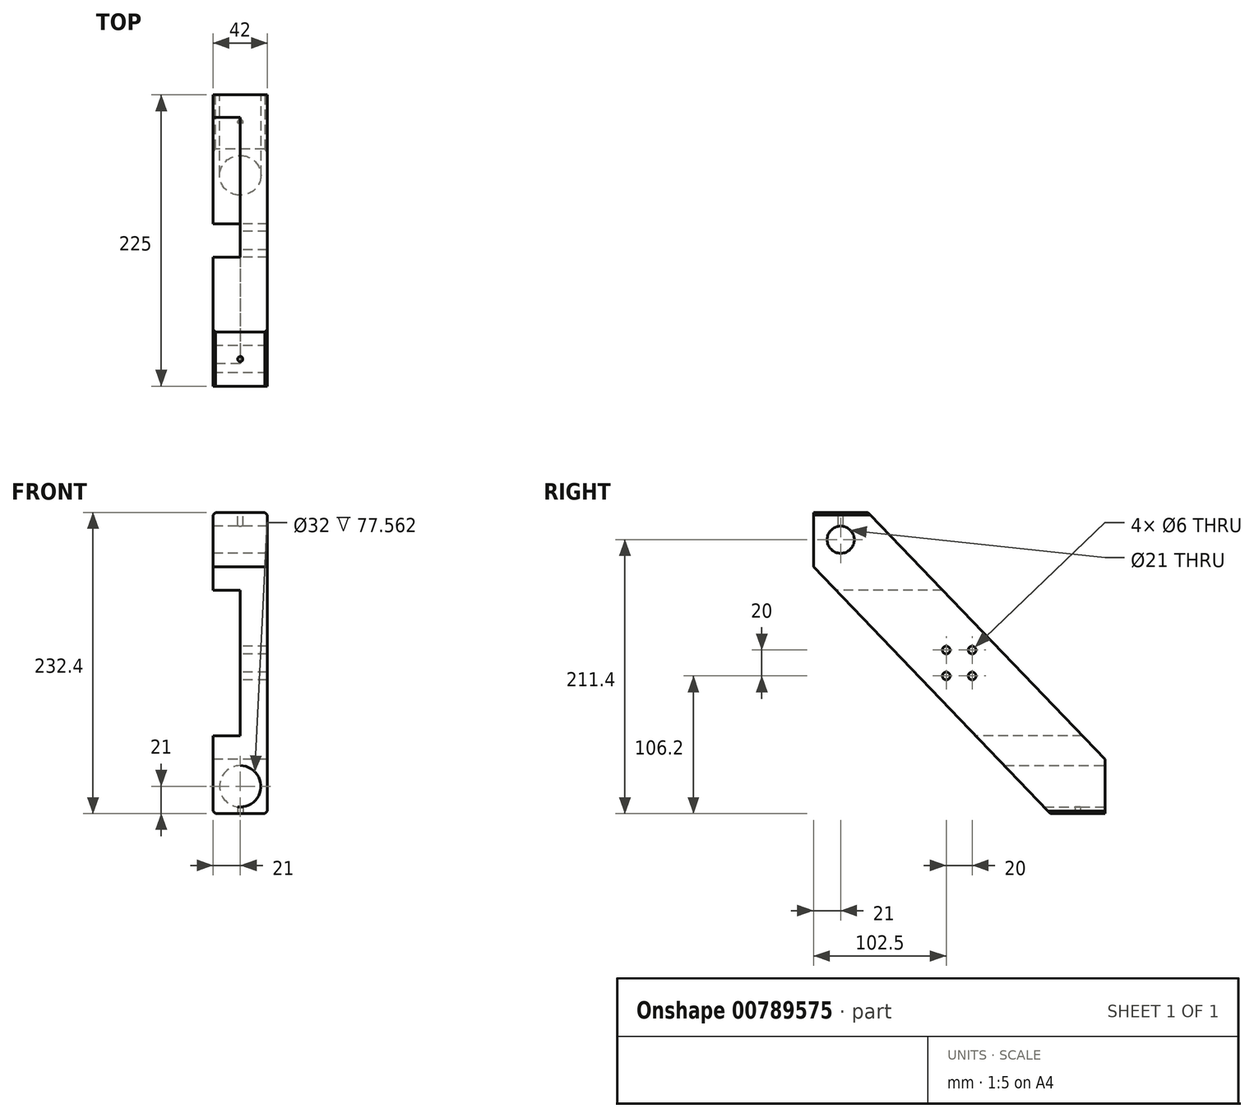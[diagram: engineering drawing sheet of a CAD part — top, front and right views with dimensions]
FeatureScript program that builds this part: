
annotation { "Feature Type Name" : "Feature", "Feature Type Description" : "" }
export const myFeature = defineFeature(function(context is Context, id is Id, definition is map)
    precondition{}
    {
        {
            var Q0;
            Q0=qCreatedBy(makeId("Right.planeOp"),FACE);
            var sketch = newSketch(context, id + "F0", { "sketchPlane" : qUnion([Q0])});
            skLineSegment(sketch, "E0.top", {"start": v(112.5, -116.2) * mm, "end": v(70.5, -116.2) * mm});
            skLineSegment(sketch, "E0.right", {"start": v(-112.5, 116.2) * mm, "end": v(-112.5, 74.2) * mm});
            skCircle(sketch, "E1", {"center": v(-91.5, 95.2) * mm, "radius": 10.5 * mm});
            skPoint(sketch, "E2", {"position": v(0, 0) * mm});
            skPoint(sketch, "E3.trimOffspring.end.orphan", {"position": v(-112.5, 116.2) * mm});
            skPoint(sketch, "E4", {"position": v(70.5, -116.2) * mm});
            skPoint(sketch, "E5", {"position": v(112.5, -74.2) * mm});
            skPoint(sketch, "E6", {"position": v(-112.5, 74.2) * mm});
            skLineSegment(sketch, "E7", {"start": v(70.5, -116.2) * mm, "end": v(-112.5, 74.2) * mm});
            skPoint(sketch, "E8", {"position": v(-70.5, 116.2) * mm});
            skLineSegment(sketch, "E9", {"start": v(112.5, -74.2) * mm, "end": v(-70.5, 116.2) * mm});
            skLineSegment(sketch, "E10.trimOffspring", {"start": v(-70.5, 116.2) * mm, "end": v(-112.5, 116.2) * mm});
            skLineSegment(sketch, "E11.trimOffspring", {"start": v(112.5, -74.2) * mm, "end": v(112.5, -116.2) * mm});
            skPoint(sketch, "E12", {"position": v(10, 10) * mm});
            skPoint(sketch, "E13", {"position": v(10, -10) * mm});
            skPoint(sketch, "E14", {"position": v(-10, -10) * mm});
            skPoint(sketch, "E15", {"position": v(-10, 10) * mm});
            skCircle(sketch, "E16", {"center": v(10, 10) * mm, "radius": 3 * mm});
            skCircle(sketch, "E17", {"center": v(-10, 10) * mm, "radius": 3 * mm});
            skCircle(sketch, "E18", {"center": v(10, -10) * mm, "radius": 3 * mm});
            skCircle(sketch, "E19", {"center": v(-10, -10) * mm, "radius": 3 * mm});
            skSolve(sketch);
        }
        {
            var Q0;
            Q0=makeQuery(id+"F0.imprint","IMPRINT",FACE,{"disambiguationData":[TD([[makeQuery(id+"F0.imprint","IMPRINT",EDGE,{"derivedFrom":sQuery(id+"F0.wireOp",EDGE,"E0.top")}),-1.0]])]});
            extrude(context, id + "F1", {"entities" : qUnion([Q0]), "depth" : 42 * mm, "offsetDistance" : 25 * mm});
        }
        {
            var Q0;
            Q0=makeQuery(id+"F0.imprint","IMPRINT",FACE,{"disambiguationData":[TD([[makeQuery(id+"F0.imprint","IMPRINT",EDGE,{"derivedFrom":sQuery(id+"F0.wireOp",EDGE,"E0.top")}),-1.0]])]});
            var sketch = newSketch(context, id + "F2", { "sketchPlane" : qUnion([Q0])});
            skLineSegment(sketch, "E20", {"start": v(95.2, -56.2) * mm, "end": v(12.83, -56.2) * mm});
            skLineSegment(sketch, "E21", {"start": v(-12.83, 56.2) * mm, "end": v(-95.2, 56.2) * mm});
            skLineSegment(sketch, "E22", {"start": v(12.83, -56.2) * mm, "end": v(-95.2, 56.2) * mm});
            skLineSegment(sketch, "E23", {"start": v(-12.83, 56.2) * mm, "end": v(95.2, -56.2) * mm});
            skSolve(sketch);
        }
        {
            var Q0;
            Q0=makeQuery(id+"F2.imprint","IMPRINT",FACE,{"disambiguationData":[TD([[makeQuery(id+"F2.imprint","IMPRINT",EDGE,{"derivedFrom":sQuery(id+"F2.wireOp",EDGE,"E20")}),-1.0]])]});
            extrude(context, id + "F3", {"entities" : qUnion([Q0]), "operationType" : NewBodyOperationType.REMOVE, "depth" : 21 * mm, "offsetDistance" : 25 * mm});
        }
        {
            var Q0;
            Q0=makeQuery(id+"F1.opExtrude","SWEPT_FACE",FACE,{"disambiguationData":[OSD([sQuery(id+"F0.wireOp",EDGE,"E11.trimOffspring")])]});
            var sketch = newSketch(context, id + "F4", { "sketchPlane" : qUnion([Q0])});
            skPoint(sketch, "E24", {"position": v(-21, -95.2) * mm});
            skPoint(sketch, "E24.positionSnap0", {"position": v(-42, -95.2) * mm});
            skPoint(sketch, "E24.positionSnap1", {"position": v(-21, -116.2) * mm});
            skCircle(sketch, "E25", {"center": v(-21, -95.2) * mm, "radius": 16 * mm});
            skSolve(sketch);
        }
        {
            var Q0;
            Q0=makeQuery(id+"F4.imprint","IMPRINT",FACE,{"disambiguationData":[TD([[makeQuery(id+"F4.imprint","IMPRINT",EDGE,{"derivedFrom":sQuery(id+"F4.wireOp",EDGE,"E25")}),1.0]])]});
            extrude(context, id + "F5", {"entities" : qUnion([Q0]), "operationType" : NewBodyOperationType.REMOVE, "oppositeDirection" : true, "depth" : 85 * mm, "offsetDistance" : 25 * mm});
        }
        {
            var Q0;
            Q0=makeQuery(id+"F3.boolean.opBoolean","COPY",EDGE,{"derivedFrom":makeQuery(id+"F3.opExtrude","CAP_EDGE",EDGE,{"disambiguationData":[OSD([sQuery(id+"F2.wireOp",EDGE,"E23")])],"isStart":false})});
            var Q1;
            Q1=makeQuery(id+"F3.boolean.opBoolean","COPY",EDGE,{"derivedFrom":makeQuery(id+"F3.opExtrude","CAP_EDGE",EDGE,{"disambiguationData":[OSD([sQuery(id+"F2.wireOp",EDGE,"E22")])],"isStart":false})});
            var Q2;
            Q2=makeQuery(id+"F3.boolean.opBoolean","COPY",EDGE,{"derivedFrom":makeQuery(id+"F3.opExtrude","CAP_EDGE",EDGE,{"disambiguationData":[OSD([sQuery(id+"F2.wireOp",EDGE,"E21")])],"isStart":true})});
            var Q3;
            Q3=makeQuery(id+"F1.opExtrude","CAP_EDGE",EDGE,{"disambiguationData":[OSD([sQuery(id+"F0.wireOp",EDGE,"E10.trimOffspring")])],"isStart":true});
            var Q4;
            Q4=makeQuery(id+"F1.opExtrude","CAP_EDGE",EDGE,{"disambiguationData":[OSD([sQuery(id+"F0.wireOp",EDGE,"E0.top")])],"isStart":true});
            var Q5;
            Q5=makeQuery(id+"F3.boolean.opBoolean","COPY",EDGE,{"derivedFrom":makeQuery(id+"F3.opExtrude","CAP_EDGE",EDGE,{"disambiguationData":[OSD([sQuery(id+"F2.wireOp",EDGE,"E20")])],"isStart":true})});
            var Q6;
            Q6=makeQuery(id+"F1.opExtrude","CAP_EDGE",EDGE,{"disambiguationData":[OSD([sQuery(id+"F0.wireOp",EDGE,"E0.top")])],"isStart":false});
            var Q7;
            Q7=makeQuery(id+"F1.opExtrude","CAP_EDGE",EDGE,{"disambiguationData":[OSD([sQuery(id+"F0.wireOp",EDGE,"E10.trimOffspring")])],"isStart":false});
            chamfer(context, id + "F6", {"entities" : qUnion([Q0, Q1, Q2, Q3, Q4, Q5, Q6, Q7]), "width" : 2 * mm, "tangentPropagation" : true});
        }
        {
            var Q0;
            Q0=makeQuery(id+"F1.opExtrude","SWEPT_FACE",FACE,{"disambiguationData":[OSD([sQuery(id+"F0.wireOp",EDGE,"E10.trimOffspring")])]});
            var sketch = newSketch(context, id + "F7", { "sketchPlane" : qUnion([Q0])});
            skPoint(sketch, "E26", {"position": v(21, -91.5) * mm});
            skPoint(sketch, "E26.positionSnap0", {"position": v(2, -91.5) * mm});
            skPoint(sketch, "E26.positionSnap1", {"position": v(21, -70.5) * mm});
            skCircle(sketch, "E27", {"center": v(21, -91.5) * mm, "radius": 2 * mm});
            skSolve(sketch);
        }
        {
            var Q0;
            Q0=makeQuery(id+"F7.imprint","IMPRINT",FACE,{"disambiguationData":[TD([[makeQuery(id+"F7.imprint","IMPRINT",EDGE,{"derivedFrom":sQuery(id+"F7.wireOp",EDGE,"E27")}),1.0]])]});
            extrude(context, id + "F8", {"entities" : qUnion([Q0]), "operationType" : NewBodyOperationType.REMOVE, "oppositeDirection" : true, "depth" : 25 * mm, "offsetDistance" : 25 * mm});
        }
        {
            var Q0;
            Q0=makeQuery(id+"F1.opExtrude","SWEPT_FACE",FACE,{"disambiguationData":[OSD([sQuery(id+"F0.wireOp",EDGE,"E0.top")])]});
            var sketch = newSketch(context, id + "F9", { "sketchPlane" : qUnion([Q0])});
            skPoint(sketch, "E28", {"position": v(21, -91.5) * mm});
            skPoint(sketch, "E28.positionSnap0", {"position": v(21, -70.5) * mm});
            skPoint(sketch, "E28.positionSnap1", {"position": v(2, -91.5) * mm});
            skCircle(sketch, "E29", {"center": v(21, -91.5) * mm, "radius": 2 * mm});
            skSolve(sketch);
        }
        {
            var Q0;
            Q0=makeQuery(id+"F9.imprint","IMPRINT",FACE,{"disambiguationData":[TD([[makeQuery(id+"F9.imprint","IMPRINT",EDGE,{"derivedFrom":sQuery(id+"F9.wireOp",EDGE,"E29")}),1.0]])]});
            extrude(context, id + "F10", {"entities" : qUnion([Q0]), "operationType" : NewBodyOperationType.REMOVE, "oppositeDirection" : true, "depth" : 25 * mm, "offsetDistance" : 25 * mm});
        }
    });
